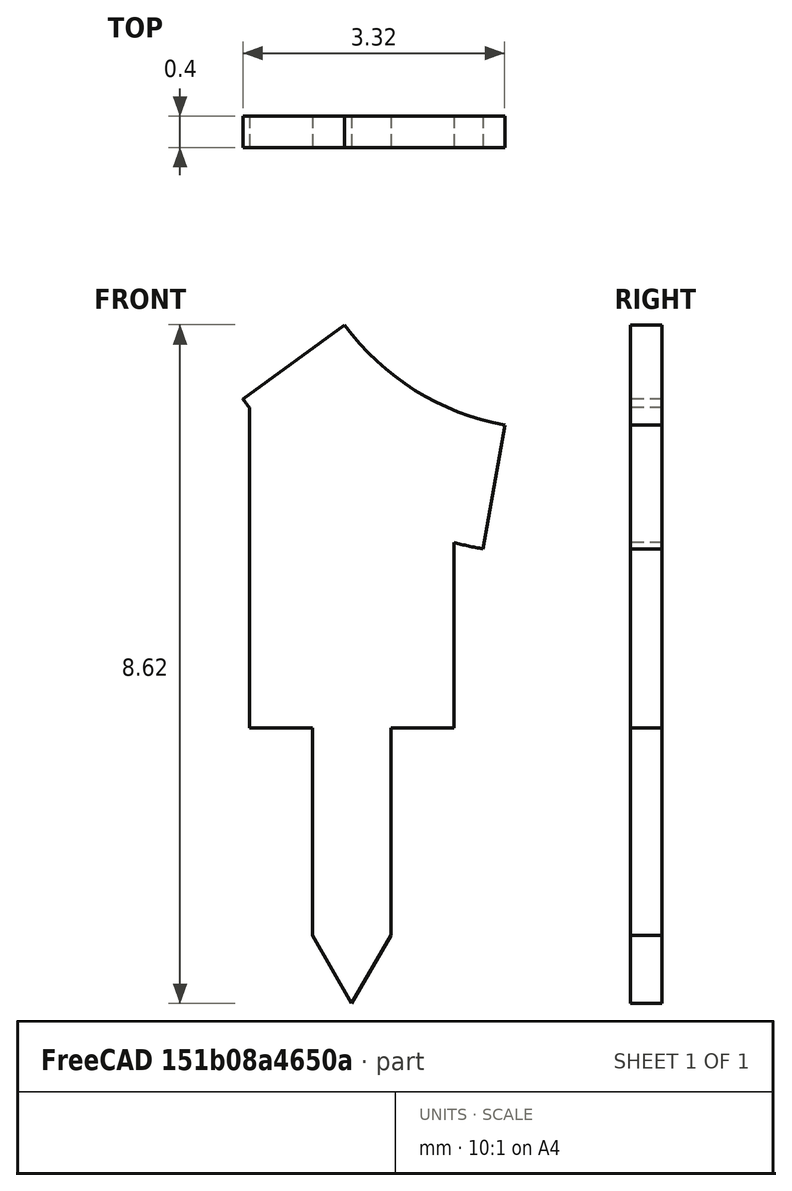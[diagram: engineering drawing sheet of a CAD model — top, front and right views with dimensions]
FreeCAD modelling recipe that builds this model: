
FCSTD DOCUMENT  (FreeCAD 0.16R6703 (Git))
Label: InitialFinal
License: CreativeCommons Attribution-ShareAlike
LicenseURL: http://creativecommons.org/licenses/by-sa/4.0/
objects: Sketcher::SketchObject×1, PartDesign::Pad×1
note: 3 computed .brp shape members not serialized (recipe doc carries the construction recipe); baked Part::Feature solids carry a one-line shape summary decoded from their .brp

FEATURE [Sketcher::SketchObject] Sketch
  Placement = pos=(0,0,0) rot=(1,0,0;1.5708rad)
  sketch-geometry (16):
    g0: LineSegment StartX=-2.5 StartY=0 StartZ=0 EndX=-3 EndY=0.866025 EndZ=0
    g1: LineSegment StartX=-2.5 StartY=0 StartZ=0 EndX=-2 EndY=0.866025 EndZ=0
    g2: LineSegment StartX=-2 StartY=0.866025 StartZ=0 EndX=-2 EndY=3.5 EndZ=0
    g3: LineSegment StartX=-3 StartY=3.5 StartZ=0 EndX=-3 EndY=0.866025 EndZ=0
    g4: LineSegment StartX=-3 StartY=3.5 StartZ=0 EndX=-3.8 EndY=3.5 EndZ=0
    g5: LineSegment [constr] StartX=0 StartY=10.5 StartZ=0 EndX=-3.88328 EndY=7.67863 EndZ=0
    g6: LineSegment StartX=-3.8 StartY=3.5 StartZ=0 EndX=-3.8 EndY=7.56742 EndZ=0
    g7: ArcOfCircle CenterX=0 CenterY=10.5 CenterZ=0 NormalX=0 NormalY=0 NormalZ=1 Radius=4.8 StartAngle=3.76991 EndAngle=3.79886
    g8: LineSegment StartX=-2 StartY=3.5 StartZ=0 EndX=-1.2 EndY=3.5 EndZ=0
    g9: LineSegment StartX=-1.2 StartY=3.5 StartZ=0 EndX=-1.2 EndY=5.85242 EndZ=0
    g10: ArcOfCircle [constr] CenterX=0 CenterY=10.5 CenterZ=0 NormalX=0 NormalY=0 NormalZ=1 Radius=4.8 StartAngle=3.76991 EndAngle=4.53786
    g11: LineSegment [constr] StartX=0 StartY=10.5 StartZ=0 EndX=-0.833511 EndY=5.77292 EndZ=0
    g12: ArcOfCircle CenterX=0 CenterY=10.5 CenterZ=0 NormalX=0 NormalY=0 NormalZ=1 Radius=3.2 StartAngle=3.76991 EndAngle=4.53786
    g13: LineSegment StartX=-3.88328 StartY=7.67863 StartZ=0 EndX=-2.58885 EndY=8.61909 EndZ=0
    g14: LineSegment StartX=-0.833511 StartY=5.77292 StartZ=0 EndX=-0.555674 EndY=7.34862 EndZ=0
    g15: ArcOfCircle CenterX=0 CenterY=10.5 CenterZ=0 NormalX=0 NormalY=0 NormalZ=1 Radius=4.8 StartAngle=4.45971 EndAngle=4.53786
  constraints (47):
    c: PointOnObject(g0,g-1)
    c: Coincident(g0,g1)
    c: Coincident(g1,g2)
    c: Vertical(g2)
    c: Coincident(g3,g0)
    c: Vertical(g3)
    c: DistanceX(g0,g-1) = 2.5
    c: Equal(g0,g1)
    c: Angle(g1,g0) = 1.0472
    c: DistanceX(g0,g1) = 1
    c: DistanceX(g1,g-1) = 2
    c: Equal(g2,g3)
    c: Coincident(g4,g3)
    c: Horizontal(g4)
    c: PointOnObject(g5,g-2)
    c: DistanceY(g-1,g5) = 10.5
    c: Coincident(g6,g4)
    c: Vertical(g6)
    c: Coincident(g7,g5)
    c: Coincident(g7,g6)
    c: Coincident(g7,g5)
    c: DistanceY(g-1,g3) = 3.5
    c: Radius(g7) = 4.8
    c: Angle(g-2,g5) = -4.08407
    c: DistanceX(g4,g4) = 0.8
    c: Coincident(g2,g8)
    c: Horizontal(g8)
    c: Coincident(g8,g9)
    c: Vertical(g9)
    c: Coincident(g10,g5)
    c: Coincident(g10,g5)
    c: DistanceX(g8,g8) = 0.8
    c: PointOnObject(g9,g10)
    c: Coincident(g11,g5)
    c: Coincident(g11,g10)
    c: Angle(g-2,g11) = 2.96706
    c: Coincident(g12,g5)
    c: PointOnObject(g12,g5)
    c: PointOnObject(g12,g11)
    c: Radius(g12) = 3.2
    c: Coincident(g13,g5)
    c: Coincident(g13,g12)
    c: Coincident(g14,g10)
    c: Coincident(g14,g12)
    c: Coincident(g15,g5)
    c: Coincident(g15,g10)
    c: Coincident(g15,g9)
FEATURE [PartDesign::Pad] Pad
  Length = 0.4
  Length2 = 100
  Placement = pos=(0,0,0) rot=(1,0,0;1.5708rad)
  Sketch = -> Sketch
  Type = 0
